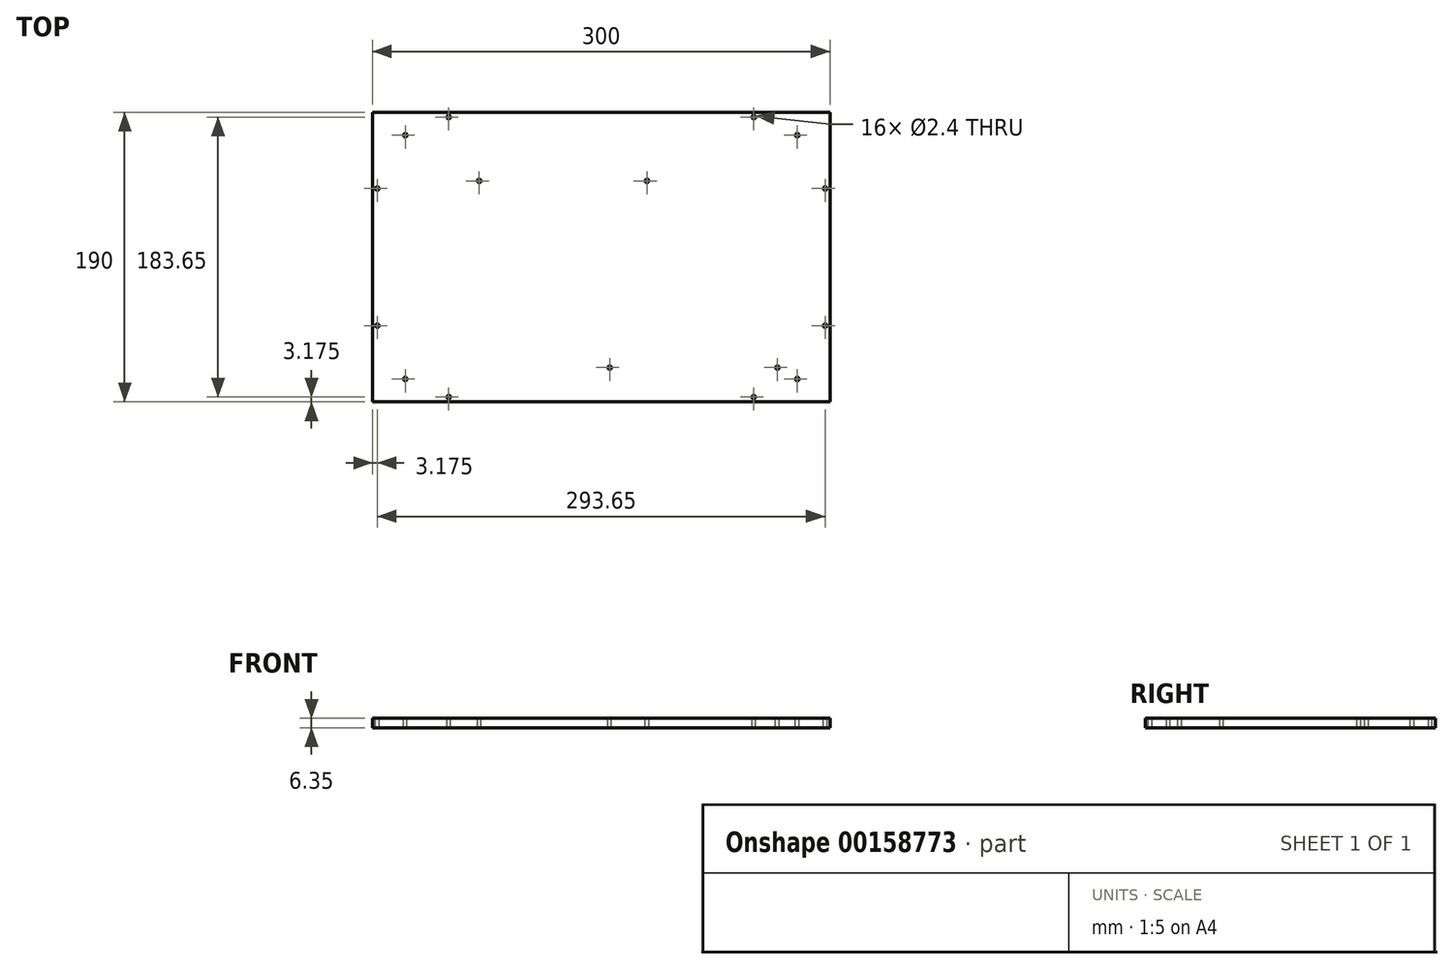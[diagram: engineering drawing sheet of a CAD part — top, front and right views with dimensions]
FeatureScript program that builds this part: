
annotation { "Feature Type Name" : "Feature", "Feature Type Description" : "" }
export const myFeature = defineFeature(function(context is Context, id is Id, definition is map)
    precondition{}
    {
        {
            var Q0;
            Q0=qCreatedBy(makeId("Top.planeOp"),FACE);
            var sketch = newSketch(context, id + "F0", { "sketchPlane" : qUnion([Q0])});
            skLineSegment(sketch, "E0.bottom", {"start": v(150, -95) * mm, "end": v(-150, -95) * mm});
            skLineSegment(sketch, "E0.top", {"start": v(150, 95) * mm, "end": v(-150, 95) * mm});
            skLineSegment(sketch, "E0.left", {"start": v(150, -95) * mm, "end": v(150, 95) * mm});
            skLineSegment(sketch, "E0.right", {"start": v(-150, -95) * mm, "end": v(-150, 95) * mm});
            skPoint(sketch, "E0.middle", {"position": v(0, 0) * mm});
            skSolve(sketch);
        }
        {
            var Q0;
            Q0 = qSketchRegion(id + "F0", true);
            extrude(context, id + "F1", {"entities" : qUnion([Q0]), "depth" : 6.35 * mm});
        }
        {
            var Q0;
            Q0=makeQuery(id+"F1.opExtrude","CAP_FACE",FACE,{"disambiguationData":[OSD([sQuery(id+"F0.wireOp",EDGE,"E0.bottom"),sQuery(id+"F0.wireOp",EDGE,"E0.top"),sQuery(id+"F0.wireOp",EDGE,"E0.left"),sQuery(id+"F0.wireOp",EDGE,"E0.right")])],"isStart":false});
            var sketch = newSketch(context, id + "F2", { "sketchPlane" : qUnion([Q0])});
            skCircle(sketch, "E1", {"center": v(-128.5, -80) * mm, "radius": 1.5 * mm});
            skCircle(sketch, "E2.MirrorC", {"center": v(128.5, -80) * mm, "radius": 1.5 * mm});
            skCircle(sketch, "E3.MirrorC", {"center": v(128.5, 80) * mm, "radius": 1.5 * mm});
            skCircle(sketch, "E4.MirrorC", {"center": v(-128.5, 80) * mm, "radius": 1.5 * mm});
            skCircle(sketch, "E5", {"center": v(5.5, -72.5) * mm, "radius": 1.5 * mm});
            skCircle(sketch, "E6", {"center": v(-80, 50) * mm, "radius": 1.5 * mm});
            skCircle(sketch, "E7.1.0.0", {"center": v(30, 50) * mm, "radius": 1.5 * mm});
            skLineSegment(sketch, "E7.direction1", {"start": v(-80, 50) * mm, "end": v(30, 50) * mm, "construction": true});
            skCircle(sketch, "E8.1.0.0", {"center": v(115.5, -72.5) * mm, "radius": 1.5 * mm});
            skLineSegment(sketch, "E8.direction1", {"start": v(5.5, -72.5) * mm, "end": v(115.5, -72.5) * mm, "construction": true});
            skSolve(sketch);
        }
        {
            var Q0;
            Q0=makeQuery(id+"F1.opExtrude","CAP_FACE",FACE,{"disambiguationData":[OSD([sQuery(id+"F0.wireOp",EDGE,"E0.bottom"),sQuery(id+"F0.wireOp",EDGE,"E0.top"),sQuery(id+"F0.wireOp",EDGE,"E0.left"),sQuery(id+"F0.wireOp",EDGE,"E0.right")])],"isStart":false});
            var sketch = newSketch(context, id + "F3", { "sketchPlane" : qUnion([Q0])});
            skCircle(sketch, "E9", {"center": v(-100, -91.83) * mm, "radius": 1.5 * mm});
            skCircle(sketch, "E10", {"center": v(-146.83, -45) * mm, "radius": 1.5 * mm});
            skCircle(sketch, "E11.MirrorC", {"center": v(100, -91.83) * mm, "radius": 1.5 * mm});
            skCircle(sketch, "E12.MirrorC", {"center": v(146.83, -45) * mm, "radius": 1.5 * mm});
            skCircle(sketch, "E13.MirrorC", {"center": v(-146.83, 45) * mm, "radius": 1.5 * mm});
            skCircle(sketch, "E14.MirrorC", {"center": v(-100, 91.83) * mm, "radius": 1.5 * mm});
            skCircle(sketch, "E15.MirrorC", {"center": v(100, 91.83) * mm, "radius": 1.5 * mm});
            skCircle(sketch, "E16.MirrorC", {"center": v(146.83, 45) * mm, "radius": 1.5 * mm});
            skSolve(sketch);
        }
        {
            var Q0;
            Q0=sQuery(id+"F2.wireOp",VERTEX,"E4.MirrorC.center");
            var Q1;
            Q1=sQuery(id+"F2.wireOp",VERTEX,"E7.direction1.start");
            var Q2;
            Q2=sQuery(id+"F2.wireOp",VERTEX,"E1.center");
            var Q3;
            Q3=sQuery(id+"F2.wireOp",VERTEX,"E8.direction1.start");
            var Q4;
            Q4=sQuery(id+"F2.wireOp",VERTEX,"E7.direction1.end");
            var Q5;
            Q5=sQuery(id+"F2.wireOp",VERTEX,"E8.direction1.end");
            var Q6;
            Q6=sQuery(id+"F2.wireOp",VERTEX,"E2.MirrorC.center");
            var Q7;
            Q7=sQuery(id+"F2.wireOp",VERTEX,"E3.MirrorC.center");
            var Q8;
            Q8=sQuery(id+"F3.wireOp",VERTEX,"E14.MirrorC.center");
            var Q9;
            Q9=sQuery(id+"F3.wireOp",VERTEX,"E13.MirrorC.center");
            var Q10;
            Q10=sQuery(id+"F3.wireOp",VERTEX,"E10.center");
            var Q11;
            Q11=sQuery(id+"F3.wireOp",VERTEX,"E9.center");
            var Q12;
            Q12=sQuery(id+"F3.wireOp",VERTEX,"E11.MirrorC.center");
            var Q13;
            Q13=sQuery(id+"F3.wireOp",VERTEX,"E12.MirrorC.center");
            var Q14;
            Q14=sQuery(id+"F3.wireOp",VERTEX,"E16.MirrorC.center");
            var Q15;
            Q15=sQuery(id+"F3.wireOp",VERTEX,"E15.MirrorC.center");
            var Q16;
            Q16=makeQuery(id+"F1.opExtrude","SWEPT_BODY",BODY,{"disambiguationData":[OSD([sQuery(id+"F0.wireOp",EDGE,"E0.bottom"),sQuery(id+"F0.wireOp",EDGE,"E0.top"),sQuery(id+"F0.wireOp",EDGE,"E0.left"),sQuery(id+"F0.wireOp",EDGE,"E0.right")])]});
            hole(context, id + "F4", {"style" : HoleStyle.SIMPLE, "endStyle" : HoleEndStyle.THROUGH, "holeDiameter" : 2.4 * mm, "locations" : qUnion([Q0, Q1, Q2, Q3, Q4, Q5, Q6, Q7, Q8, Q9, Q10, Q11, Q12, Q13, Q14, Q15]), "scope" : qUnion([Q16]), "isTappedThrough" : true});
        }
    });
